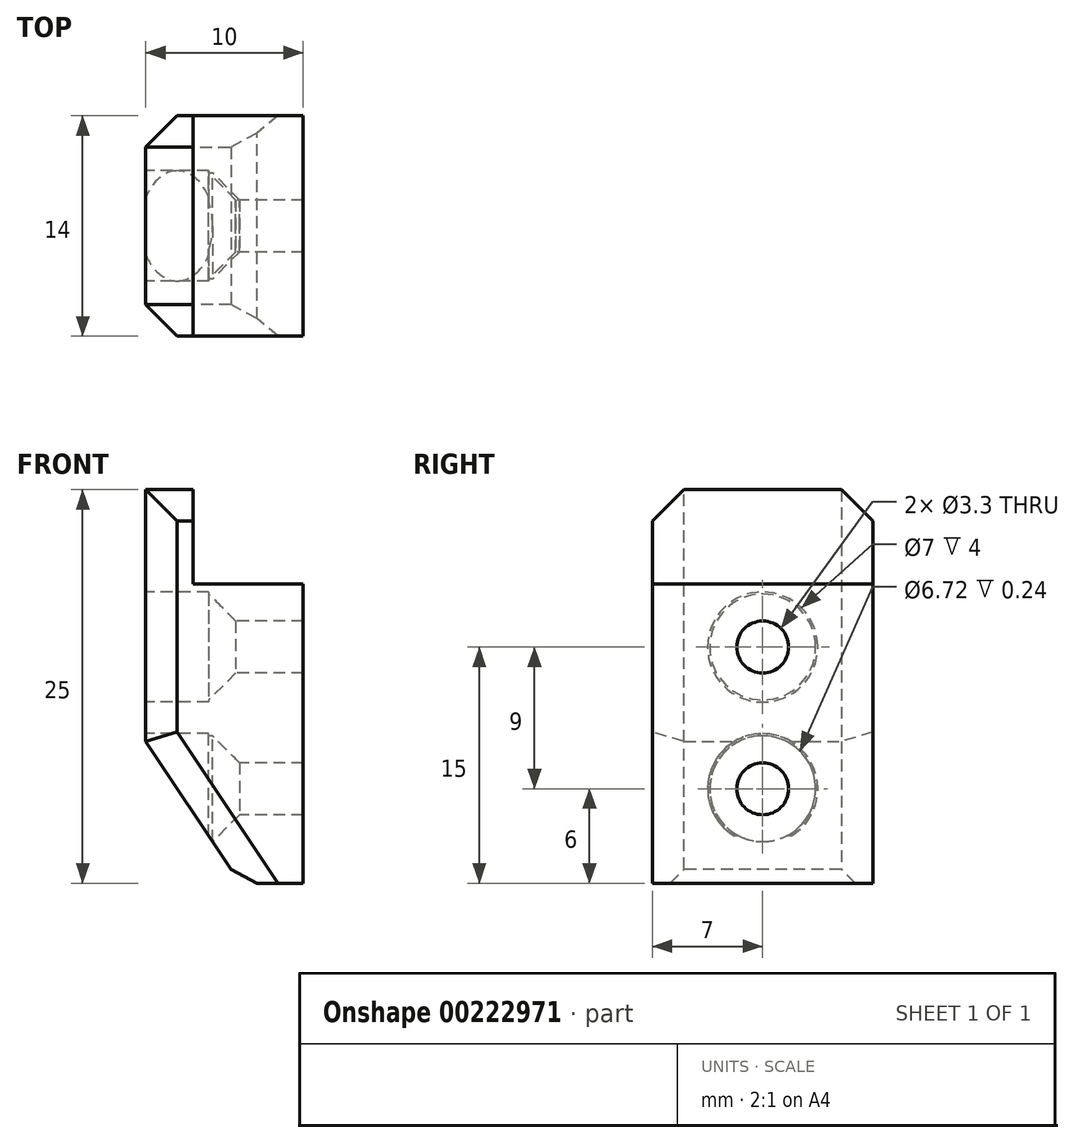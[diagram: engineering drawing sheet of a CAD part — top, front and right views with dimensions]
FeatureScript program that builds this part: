
annotation { "Feature Type Name" : "Feature", "Feature Type Description" : "" }
export const myFeature = defineFeature(function(context is Context, id is Id, definition is map)
    precondition{}
    {
        {
            var Q0;
            Q0=qCreatedBy(makeId("Front.planeOp"),FACE);
            var sketch = newSketch(context, id + "F0", { "sketchPlane" : qUnion([Q0])});
            skLineSegment(sketch, "E0", {"start": v(0, 0) * mm, "end": v(-10, 0) * mm});
            skLineSegment(sketch, "E1", {"start": v(-10, 0) * mm, "end": v(-10, -16) * mm});
            skLineSegment(sketch, "E2", {"start": v(-10, -16) * mm, "end": v(-4, -25) * mm});
            skLineSegment(sketch, "E3", {"start": v(-4, -25) * mm, "end": v(0, -25) * mm});
            skLineSegment(sketch, "E4", {"start": v(0, -25) * mm, "end": v(0, 0) * mm});
            skSolve(sketch);
        }
        {
            var Q0;
            Q0=makeQuery(id+"F0.imprint","IMPRINT",FACE,{"disambiguationData":[TD([[makeQuery(id+"F0.imprint","IMPRINT",EDGE,{"derivedFrom":sQuery(id+"F0.wireOp",EDGE,"E0")}),1.0]])]});
            extrude(context, id + "F1", {"entities" : qUnion([Q0]), "endBound" : BoundingType.SYMMETRIC, "depth" : 14 * mm});
        }
        {
            var Q0;
            Q0=makeQuery(id+"F1.opExtrude","SWEPT_FACE",FACE,{"disambiguationData":[OSD([sQuery(id+"F0.wireOp",EDGE,"E1")])]});
            var sketch = newSketch(context, id + "F2", { "sketchPlane" : qUnion([Q0])});
            skLineSegment(sketch, "E5.0", {"start": v(7, 0) * mm, "end": v(-7, 0) * mm, "construction": true});
            skCircle(sketch, "E6", {"center": v(0, -10) * mm, "radius": 3.5 * mm});
            skCircle(sketch, "E7", {"center": v(0, -19) * mm, "radius": 3.5 * mm});
            skSolve(sketch);
        }
        {
            var Q0;
            Q0=qSketchRegion(id+"F2",true);
            extrude(context, id + "F3", {"entities" : qUnion([Q0]), "operationType" : NewBodyOperationType.REMOVE, "oppositeDirection" : true, "depth" : 4 * mm});
        }
        {
            var Q0;
            Q0=sQuery(id+"F2.wireOp",VERTEX,"E7.center");
            var Q1;
            Q1=sQuery(id+"F2.wireOp",VERTEX,"E6.center");
            var Q2;
            Q2=makeQuery(id+"F1.opExtrude","SWEPT_BODY",BODY,{"disambiguationData":[OSD([sQuery(id+"F0.wireOp",EDGE,"E0"),sQuery(id+"F0.wireOp",EDGE,"E1"),sQuery(id+"F0.wireOp",EDGE,"E2"),sQuery(id+"F0.wireOp",EDGE,"E3"),sQuery(id+"F0.wireOp",EDGE,"E4")])]});
            hole(context, id + "F4", {"style" : HoleStyle.C_SINK, "endStyle" : HoleEndStyle.THROUGH, "standardTappedOrClearance" : lookupTablePath({ "standard" : "ISO", "fit" : "Normal", "size" : "M3", "type" : "Clearance" }), "standardBlindInLast" : lookupTablePath({ "fit" : "Standard", "standard" : "ISO", "size" : "M3", "type" : "Clearance" }), "holeDiameter" : 3.3 * mm, "cSinkDiameter" : 6.72 * mm, "cSinkAngle" : 90 * degree, "locations" : qUnion([Q0, Q1]), "scope" : qUnion([Q2]), "isTappedThrough" : true});
        }
        {
            var Q0;
            Q0=makeQuery(id+"F1.opExtrude","CAP_EDGE",EDGE,{"disambiguationData":[OSD([sQuery(id+"F0.wireOp",EDGE,"E0")])],"isStart":false});
            var Q1;
            Q1=makeQuery(id+"F1.opExtrude","CAP_EDGE",EDGE,{"disambiguationData":[OSD([sQuery(id+"F0.wireOp",EDGE,"E0")])],"isStart":true});
            var Q2;
            Q2=makeQuery(id+"F1.opExtrude","CAP_EDGE",EDGE,{"disambiguationData":[OSD([sQuery(id+"F0.wireOp",EDGE,"E1")])],"isStart":true});
            var Q3;
            Q3=makeQuery(id+"F1.opExtrude","CAP_EDGE",EDGE,{"disambiguationData":[OSD([sQuery(id+"F0.wireOp",EDGE,"E1")])],"isStart":false});
            var Q4;
            Q4=makeQuery(id+"F1.opExtrude","CAP_EDGE",EDGE,{"disambiguationData":[OSD([sQuery(id+"F0.wireOp",EDGE,"E2")])],"isStart":false});
            var Q5;
            Q5=makeQuery(id+"F1.opExtrude","CAP_EDGE",EDGE,{"disambiguationData":[OSD([sQuery(id+"F0.wireOp",EDGE,"E2")])],"isStart":true});
            var Q6;
            Q6=makeQuery(id+"F1.opExtrude","SWEPT_EDGE",EDGE,{"disambiguationData":[OSD([sQuery(id+"F0.wireOp",EDGE,"E2"),sQuery(id+"F0.wireOp",EDGE,"E3")])]});
            chamfer(context, id + "F5", {"entities" : qUnion([Q0, Q1, Q2, Q3, Q4, Q5, Q6]), "width" : 2 * mm, "tangentPropagation" : true});
        }
        {
            var Q0;
            Q0=qCreatedBy(makeId("Front.planeOp"),FACE);
            var sketch = newSketch(context, id + "F6", { "sketchPlane" : qUnion([Q0])});
            skLineSegment(sketch, "E8.bottom", {"start": v(0, -6) * mm, "end": v(-7, -6) * mm});
            skLineSegment(sketch, "E8.top", {"start": v(0, 0) * mm, "end": v(-7, 0) * mm});
            skLineSegment(sketch, "E8.left", {"start": v(0, -6) * mm, "end": v(0, 0) * mm});
            skLineSegment(sketch, "E8.right", {"start": v(-7, -6) * mm, "end": v(-7, 0) * mm});
            skSolve(sketch);
        }
        {
            var Q0;
            Q0=qSketchRegion(id+"F6",true);
            extrude(context, id + "F7", {"entities" : qUnion([Q0]), "operationType" : NewBodyOperationType.REMOVE, "endBound" : BoundingType.THROUGH_ALL, "oppositeDirection" : true, "depth" : 25 * mm, "hasSecondDirection" : true, "secondDirectionBound" : SecondDirectionBoundingType.THROUGH_ALL, "secondDirectionOppositeDirection" : false, "secondDirectionDepth" : 25 * mm});
        }
    });
